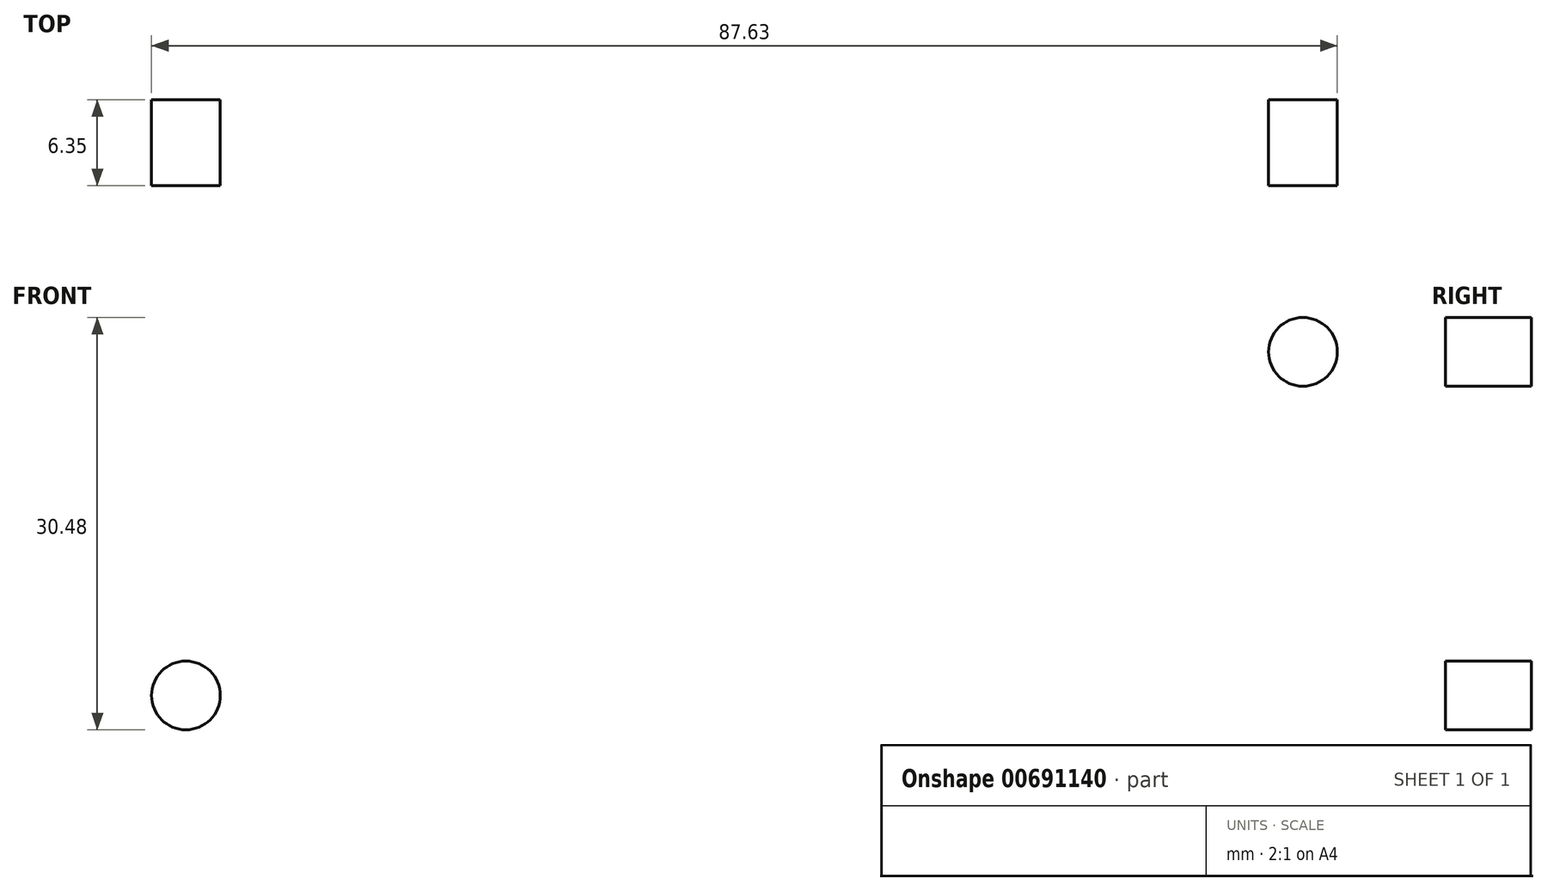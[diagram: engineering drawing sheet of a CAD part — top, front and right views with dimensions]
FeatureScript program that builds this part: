
annotation { "Feature Type Name" : "Feature", "Feature Type Description" : "" }
export const myFeature = defineFeature(function(context is Context, id is Id, definition is map)
    precondition{}
    {
        {
            var Q0;
            Q0=qCreatedBy(makeId("Front.planeOp"),FACE);
            var sketch = newSketch(context, id + "F0", { "sketchPlane" : qUnion([Q0])});
            skLineSegment(sketch, "E0", {"start": v(0, 0) * mm, "end": v(152.4, 0) * mm});
            skLineSegment(sketch, "E1", {"start": v(0, 0) * mm, "end": v(0, 50.8) * mm, "construction": true});
            skLineSegment(sketch, "E2", {"start": v(152.4, 0) * mm, "end": v(152.4, 50.8) * mm, "construction": true});
            skLineSegment(sketch, "E3", {"start": v(0, 50.8) * mm, "end": v(152.4, 50.8) * mm, "construction": true});
            skLineSegment(sketch, "E4", {"start": v(76.2, 50.8) * mm, "end": v(76.2, 76.2) * mm, "construction": true});
            skCircle(sketch, "E5", {"center": v(76.2, 76.2) * mm, "radius": 14.29 * mm});
            skCircle(sketch, "E6", {"center": v(76.2, 76.2) * mm, "radius": 25.4 * mm, "construction": true});
            skLineSegment(sketch, "E7", {"start": v(0, 50.8) * mm, "end": v(60.96, 96.52) * mm, "construction": true});
            skLineSegment(sketch, "E8.MirrorCS", {"start": v(152.4, 50.8) * mm, "end": v(91.44, 96.52) * mm, "construction": true});
            skArc(sketch, "E9", {"start": v(60.96, 96.52) * mm, "mid": v(76.2, 101.6) * mm, "end": v(91.44, 96.52) * mm});
            skLineSegment(sketch, "E10", {"start": v(0, 0) * mm, "end": v(0, 38.1) * mm});
            skLineSegment(sketch, "E11", {"start": v(60.96, 96.52) * mm, "end": v(10.16, 58.42) * mm});
            skPoint(sketch, "E12.visualSharp", {"position": v(0, 50.8) * mm});
            skArc(sketch, "E12.filletArc", {"start": v(10.16, 58.42) * mm, "mid": v(2.68, 49.46) * mm, "end": v(0, 38.1) * mm});
            skArc(sketch, "E13.MirrorCS", {"start": v(142.24, 58.42) * mm, "mid": v(149.72, 49.46) * mm, "end": v(152.4, 38.1) * mm});
            skLineSegment(sketch, "E14.MirrorCS", {"start": v(91.44, 96.52) * mm, "end": v(142.24, 58.42) * mm});
            skLineSegment(sketch, "E15.MirrorCS", {"start": v(152.4, 0) * mm, "end": v(152.4, 38.1) * mm});
            skSolve(sketch);
        }
        {
            var Q0;
            Q0=makeQuery(id+"F0.imprint","IMPRINT",FACE,{"disambiguationData":[TD([[makeQuery(id+"F0.imprint","IMPRINT",EDGE,{"derivedFrom":sQuery(id+"F0.wireOp",EDGE,"E0")}),1.0]])]});
            extrude(context, id + "F1", {"entities" : qUnion([Q0]), "depth" : 6.35 * mm, "offsetDistance" : 25.4 * mm});
        }
        {
            var Q0;
            Q0=makeQuery(id+"F1.opExtrude","CAP_FACE",FACE,{"disambiguationData":[OSD([sQuery(id+"F0.wireOp",EDGE,"E0"),sQuery(id+"F0.wireOp",EDGE,"E5"),sQuery(id+"F0.wireOp",EDGE,"E9"),sQuery(id+"F0.wireOp",EDGE,"E10"),sQuery(id+"F0.wireOp",EDGE,"E11"),sQuery(id+"F0.wireOp",EDGE,"E12.filletArc"),sQuery(id+"F0.wireOp",EDGE,"E13.MirrorCS"),sQuery(id+"F0.wireOp",EDGE,"E14.MirrorCS"),sQuery(id+"F0.wireOp",EDGE,"E15.MirrorCS")])],"isStart":false});
            var sketch = newSketch(context, id + "F2", { "sketchPlane" : qUnion([Q0])});
            skLineSegment(sketch, "E16", {"start": v(0, 25.4) * mm, "end": v(152.4, 25.4) * mm, "construction": true});
            skLineSegment(sketch, "E17", {"start": v(0, 38.1) * mm, "end": v(152.4, 38.1) * mm, "construction": true});
            skCircle(sketch, "E18", {"center": v(12.93, 38.1) * mm, "radius": 2.54 * mm});
            skLineSegment(sketch, "E19", {"start": v(76.2, 0) * mm, "end": v(76.2, 61.91) * mm, "construction": true});
            skCircle(sketch, "E20", {"center": v(34.92, 25.4) * mm, "radius": 34.93 * mm, "construction": true});
            skCircle(sketch, "E21", {"center": v(34.92, 25.4) * mm, "radius": 25.4 * mm, "construction": true});
            skLineSegment(sketch, "E22", {"start": v(12.93, 38.1) * mm, "end": v(34.93, 25.4) * mm, "construction": true});
            skLineSegment(sketch, "E23", {"start": v(34.92, 25.4) * mm, "end": v(22.22, 3.4) * mm, "construction": true});
            skCircle(sketch, "E24.MirrorC", {"center": v(56.92, 12.7) * mm, "radius": 2.54 * mm});
            skCircle(sketch, "E25.MirrorC", {"center": v(139.47, 38.1) * mm, "radius": 2.54 * mm});
            skCircle(sketch, "E26.MirrorC", {"center": v(95.48, 12.7) * mm, "radius": 2.54 * mm});
            skSolve(sketch);
        }
        {
            var Q0;
            Q0=makeQuery(id+"F2.imprint","IMPRINT",FACE,{"disambiguationData":[TD([[makeQuery(id+"F2.imprint","IMPRINT",EDGE,{"derivedFrom":sQuery(id+"F2.wireOp",EDGE,"E18")}),1.0]])]});
            var Q1;
            Q1=makeQuery(id+"F2.imprint","IMPRINT",FACE,{"disambiguationData":[TD([[makeQuery(id+"F2.imprint","IMPRINT",EDGE,{"derivedFrom":sQuery(id+"F2.wireOp",EDGE,"E24.MirrorC")}),-1.0]])]});
            var Q2;
            Q2=makeQuery(id+"F2.imprint","IMPRINT",FACE,{"disambiguationData":[TD([[makeQuery(id+"F2.imprint","IMPRINT",EDGE,{"derivedFrom":sQuery(id+"F2.wireOp",EDGE,"E26.MirrorC")}),1.0]])]});
            var Q3;
            Q3=makeQuery(id+"F2.imprint","IMPRINT",FACE,{"disambiguationData":[TD([[makeQuery(id+"F2.imprint","IMPRINT",EDGE,{"derivedFrom":sQuery(id+"F2.wireOp",EDGE,"E25.MirrorC")}),-1.0]])]});
            extrude(context, id + "F3", {"entities" : qUnion([Q0, Q1, Q2, Q3]), "operationType" : NewBodyOperationType.REMOVE, "endBound" : BoundingType.THROUGH_ALL, "oppositeDirection" : true, "depth" : 25.4 * mm, "offsetDistance" : 25.4 * mm});
        }
    });
